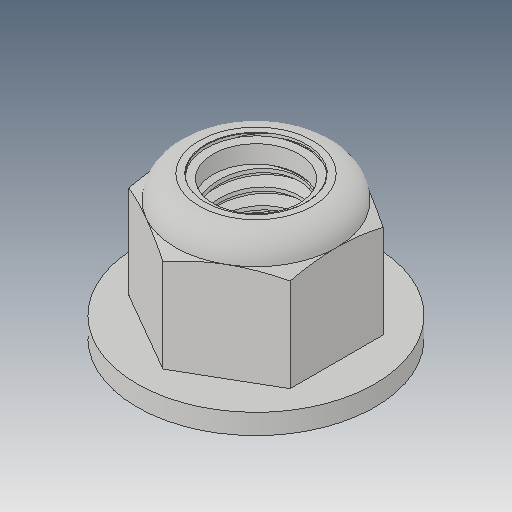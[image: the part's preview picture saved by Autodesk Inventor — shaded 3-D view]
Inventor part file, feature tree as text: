
AUTODESK INVENTOR PART (.ipt)
format: ipt  version: 2018 (Build 220112000, 112)  size: 317,952 bytes
history: native  units: in
note: dims shown in document units (in); Inventor stores cm internally (conversion verified against a paired STEP export)
features: other x1, revolve x1
ambient origin geometry x8: Origin, YZ Plane, XZ Plane, XY Plane, X Axis, Y Axis, Z Axis, Center Point
bodies: Solid1 (feature_tree), Solid2 (feature_tree)
feature tree (2):
  other  "Cut-Revolve4"
  revolve  "Revolve2"  [1 undecoded]
note: 1 required parameter value undecoded (feature->parameter linkage not recoverable at this tier; creation-order binding heuristic only, values carry confidence <= 0.55)
